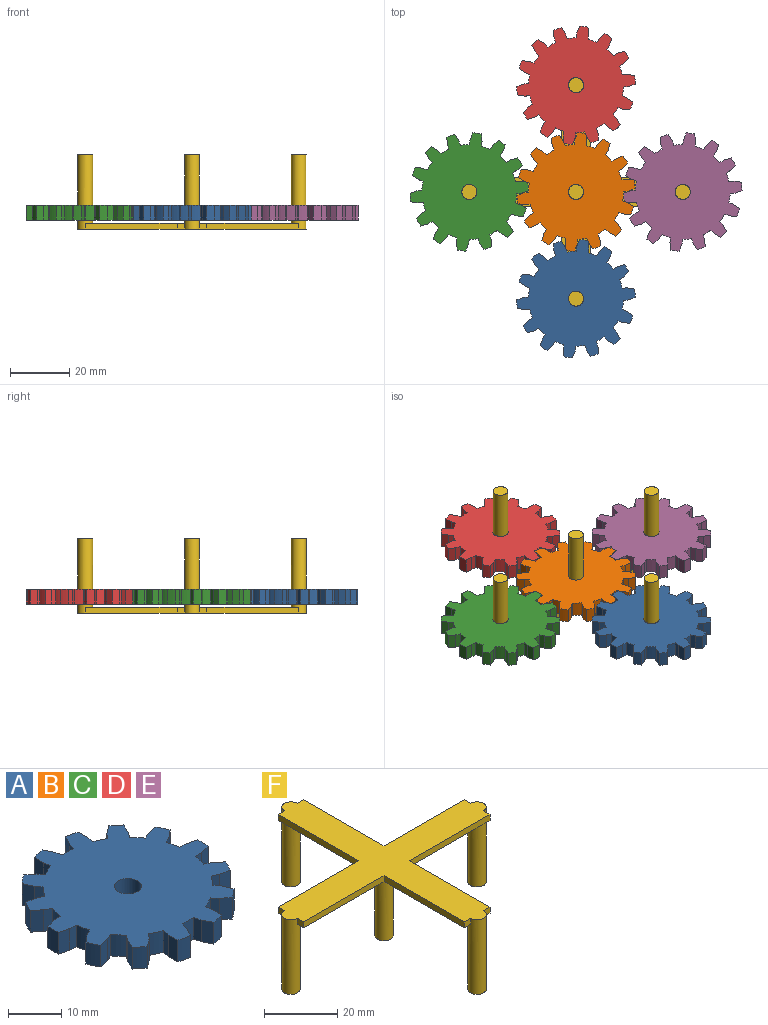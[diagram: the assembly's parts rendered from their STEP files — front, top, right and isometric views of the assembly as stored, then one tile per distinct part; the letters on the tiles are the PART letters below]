
ASSEMBLY  parts=6 mates=5
PART A: 87 faces, bbox 40x39.5x5 mm
  f0: cylinder r=20mm len=5mm, axis (0,0,-1), area 14.3mm2, adj f15,f16,f19,f83
  f1: cylinder r=20mm len=5mm, axis (0,0,-1), area 14.3mm2, adj f15,f16,f78,f84
  f2: cylinder r=20mm len=5mm, axis (0,0,-1), area 14.3mm2, adj f15,f16,f73,f79
  f3: cylinder r=20mm len=5mm, axis (0,0,-1), area 14.3mm2, adj f15,f16,f68,f74
  f4: cylinder r=20mm len=5mm, axis (0,0,-1), area 14.3mm2, adj f15,f16,f63,f69
  f5: cylinder r=20mm len=5mm, axis (0,0,-1), area 14.3mm2, adj f15,f16,f58,f64
  f6: cylinder r=20mm len=5mm, axis (0,0,-1), area 14.3mm2, adj f15,f16,f53,f59
  f7: cylinder r=20mm len=5mm, axis (0,0,-1), area 14.3mm2, adj f15,f16,f48,f54
  f8: cylinder r=20mm len=5mm, axis (0,0,-1), area 14.3mm2, adj f15,f16,f43,f49
  f9: cylinder r=20mm len=5mm, axis (0,0,-1), area 14.3mm2, adj f15,f16,f38,f44
  f10: cylinder r=20mm len=5mm, axis (0,0,-1), area 14.3mm2, adj f15,f16,f33,f39
  f11: cylinder r=20mm len=5mm, axis (0,0,-1), area 14.3mm2, adj f15,f16,f28,f34
  f12: cylinder r=20mm len=5mm, axis (0,0,-1), area 14.3mm2, adj f15,f16,f23,f29
  f13: cylinder r=20mm len=5mm, axis (0,0,-1), area 14.3mm2, adj f15,f16,f18,f24
  f14: cylinder r=2.55mm len=5.1mm, axis (0,0,-1), area 80.1mm2, adj f15,f16
  f15: plane 40x39.53mm, normal (0,0,1), area 993.6mm2, adj f0,f1,f2,f3,f4,f5,f6,f7
  f16: plane 40x39.53mm, normal (0,0,-1), area 993.6mm2, adj f0,f1,f2,f3,f4,f5,f6,f7
  f17: plane 5x1.64mm, normal (-0.97,0.25,0), area 8.5mm2, adj f15,f16,f18,f21
  f18: plane 5x2.19mm, normal (-0.89,0.46,0), area 12.3mm2, adj f13,f15,f16,f17
  f19: plane 5x2.19mm, normal (0.89,0.46,0), area 12.3mm2, adj f0,f15,f16,f20
  f20: plane 5x1.64mm, normal (0.97,0.25,0), area 8.5mm2, adj f15,f16,f19,f21
  f21: cylinder r=16mm len=5mm, axis (0,0,-1), area 15mm2, adj f15,f16,f17,f20
  f22: plane 5x1.3mm, normal (-0.77,0.64,0), area 8.5mm2, adj f15,f16,f23,f26
  f23: plane 5x1.97mm, normal (-0.6,0.8,0), area 12.3mm2, adj f12,f15,f16,f22
  f24: plane 5x2.47mm, normal (1,0.03,0), area 12.3mm2, adj f13,f15,f16,f25
  f25: plane 5x1.66mm, normal (0.98,-0.2,0), area 8.5mm2, adj f15,f16,f24,f26
  f26: cylinder r=16mm len=5mm, axis (0,0,-1), area 15mm2, adj f15,f16,f22,f25
  f27: plane 5x1.55mm, normal (-0.41,0.91,0), area 8.5mm2, adj f15,f16,f28,f31
  f28: plane 5x2.42mm, normal (-0.2,0.98,0), area 12.3mm2, adj f11,f15,f16,f27
  f29: plane 5x2.25mm, normal (0.91,-0.41,0), area 12.3mm2, adj f12,f15,f16,f30
  f30: plane 5x1.35mm, normal (0.8,-0.6,0), area 8.5mm2, adj f15,f16,f29,f31
  f31: cylinder r=16mm len=5mm, axis (0,0,-1), area 15mm2, adj f15,f16,f27,f30
  f32: plane 5x1.69mm, normal (0.03,1,0), area 8.5mm2, adj f15,f16,f33,f36
  f33: plane 5x2.39mm, normal (0.25,0.97,0), area 12.3mm2, adj f10,f15,f16,f32
  f34: plane 5x1.89mm, normal (0.64,-0.76,0), area 12.3mm2, adj f11,f15,f16,f35
  f35: plane 5x1.51mm, normal (0.46,-0.89,0), area 8.5mm2, adj f15,f16,f34,f36
  f36: cylinder r=16mm len=5mm, axis (0,0,-1), area 15mm2, adj f15,f16,f32,f35
  f37: plane 5x1.51mm, normal (0.46,0.89,0), area 8.5mm2, adj f15,f16,f38,f41
  f38: plane 5x1.89mm, normal (0.64,0.76,0), area 12.3mm2, adj f9,f15,f16,f37
  f39: plane 5x2.39mm, normal (0.25,-0.97,0), area 12.3mm2, adj f10,f15,f16,f40
  f40: plane 5x1.69mm, normal (0.03,-1,0), area 8.5mm2, adj f15,f16,f39,f41
  f41: cylinder r=16mm len=5mm, axis (0,0,-1), area 15mm2, adj f15,f16,f37,f40
  f42: plane 5x1.35mm, normal (0.8,0.6,0), area 8.5mm2, adj f15,f16,f43,f46
  f43: plane 5x2.25mm, normal (0.91,0.41,0), area 12.3mm2, adj f8,f15,f16,f42
  f44: plane 5x2.42mm, normal (-0.2,-0.98,0), area 12.3mm2, adj f9,f15,f16,f45
  f45: plane 5x1.55mm, normal (-0.41,-0.91,0), area 8.5mm2, adj f15,f16,f44,f46
  f46: cylinder r=16mm len=5mm, axis (0,0,-1), area 15mm2, adj f15,f16,f42,f45
  f47: plane 5x1.66mm, normal (0.98,0.2,0), area 8.5mm2, adj f15,f16,f48,f51
  f48: plane 5x2.47mm, normal (1,-0.03,0), area 12.3mm2, adj f7,f15,f16,f47
  f49: plane 5x1.97mm, normal (-0.6,-0.8,0), area 12.3mm2, adj f8,f15,f16,f50
  f50: plane 5x1.3mm, normal (-0.77,-0.64,0), area 8.5mm2, adj f15,f16,f49,f51
  f51: cylinder r=16mm len=5mm, axis (0,0,-1), area 15mm2, adj f15,f16,f47,f50
  f52: plane 5x1.64mm, normal (0.97,-0.25,0), area 8.5mm2, adj f15,f16,f53,f56
  f53: plane 5x2.19mm, normal (0.89,-0.46,0), area 12.3mm2, adj f6,f15,f16,f52
  f54: plane 5x2.19mm, normal (-0.89,-0.46,0), area 12.3mm2, adj f7,f15,f16,f55
  f55: plane 5x1.64mm, normal (-0.97,-0.25,0), area 8.5mm2, adj f15,f16,f54,f56
  f56: cylinder r=16mm len=5mm, axis (0,0,-1), area 15mm2, adj f15,f16,f52,f55
  f57: plane 5x1.3mm, normal (0.77,-0.64,0), area 8.5mm2, adj f15,f16,f58,f61
  f58: plane 5x1.97mm, normal (0.6,-0.8,0), area 12.3mm2, adj f5,f15,f16,f57
  f59: plane 5x2.47mm, normal (-1,-0.03,0), area 12.3mm2, adj f6,f15,f16,f60
  f60: plane 5x1.66mm, normal (-0.98,0.2,0), area 8.5mm2, adj f15,f16,f59,f61
  f61: cylinder r=16mm len=5mm, axis (0,0,-1), area 15mm2, adj f15,f16,f57,f60
  f62: plane 5x1.55mm, normal (0.41,-0.91,0), area 8.5mm2, adj f15,f16,f63,f66
  f63: plane 5x2.42mm, normal (0.2,-0.98,0), area 12.3mm2, adj f4,f15,f16,f62
  f64: plane 5x2.25mm, normal (-0.91,0.41,0), area 12.3mm2, adj f5,f15,f16,f65
  f65: plane 5x1.35mm, normal (-0.8,0.6,0), area 8.5mm2, adj f15,f16,f64,f66
  f66: cylinder r=16mm len=5mm, axis (0,0,-1), area 15mm2, adj f15,f16,f62,f65
  f67: plane 5x1.69mm, normal (-0.03,-1,0), area 8.5mm2, adj f15,f16,f68,f71
  f68: plane 5x2.39mm, normal (-0.25,-0.97,0), area 12.3mm2, adj f3,f15,f16,f67
  f69: plane 5x1.89mm, normal (-0.64,0.76,0), area 12.3mm2, adj f4,f15,f16,f70
  f70: plane 5x1.51mm, normal (-0.46,0.89,0), area 8.5mm2, adj f15,f16,f69,f71
  f71: cylinder r=16mm len=5mm, axis (0,0,-1), area 15mm2, adj f15,f16,f67,f70
  f72: plane 5x1.51mm, normal (-0.46,-0.89,0), area 8.5mm2, adj f15,f16,f73,f76
  f73: plane 5x1.89mm, normal (-0.64,-0.76,0), area 12.3mm2, adj f2,f15,f16,f72
  f74: plane 5x2.39mm, normal (-0.25,0.97,0), area 12.3mm2, adj f3,f15,f16,f75
  f75: plane 5x1.69mm, normal (-0.03,1,0), area 8.5mm2, adj f15,f16,f74,f76
  f76: cylinder r=16mm len=5mm, axis (0,0,-1), area 15mm2, adj f15,f16,f72,f75
  f77: plane 5x1.35mm, normal (-0.8,-0.6,0), area 8.5mm2, adj f15,f16,f78,f81
  f78: plane 5x2.25mm, normal (-0.91,-0.41,0), area 12.3mm2, adj f1,f15,f16,f77
  f79: plane 5x2.42mm, normal (0.2,0.98,0), area 12.3mm2, adj f2,f15,f16,f80
  f80: plane 5x1.55mm, normal (0.41,0.91,0), area 8.5mm2, adj f15,f16,f79,f81
  f81: cylinder r=16mm len=5mm, axis (0,0,-1), area 15mm2, adj f15,f16,f77,f80
  f82: plane 5x1.66mm, normal (-0.98,-0.2,0), area 8.5mm2, adj f15,f16,f83,f86
  f83: plane 5x2.47mm, normal (-1,0.03,0), area 12.3mm2, adj f0,f15,f16,f82
  f84: plane 5x1.97mm, normal (0.6,0.8,0), area 12.3mm2, adj f1,f15,f16,f85
  f85: plane 5x1.3mm, normal (0.77,0.64,0), area 8.5mm2, adj f15,f16,f84,f86
  f86: cylinder r=16mm len=5mm, axis (0,0,-1), area 15mm2, adj f15,f16,f82,f85
PART B: same geometry as A
PART C: same geometry as A
PART D: same geometry as A
PART E: same geometry as A
PART F: 28 faces, bbox 77x77x25 mm
  f0: plane 31x2mm, normal (1,0,0), area 62mm2, adj f1,f15,f16,f17
  f1: plane 2.5x2mm, normal (0,-1,0), area 5mm2, adj f0,f16,f17,f22
  f2: plane 2.5x2mm, normal (0,-1,0), area 5mm2, adj f3,f16,f17,f22
  f3: plane 31x2mm, normal (-1,0,0), area 62mm2, adj f2,f4,f16,f17
  f4: plane 31x2mm, normal (0,-1,0), area 62mm2, adj f3,f5,f16,f17
  f5: plane 2.5x2mm, normal (-1,0,0), area 5mm2, adj f4,f16,f17,f18
  f6: plane 2.5x2mm, normal (-1,0,0), area 5mm2, adj f7,f16,f17,f18
  f7: plane 31x2mm, normal (0,1,0), area 62mm2, adj f6,f8,f16,f17
  f8: plane 31x2mm, normal (-1,0,0), area 62mm2, adj f7,f9,f16,f17
  f9: plane 2.5x2mm, normal (0,1,0), area 5mm2, adj f8,f16,f17,f24
  f10: plane 2.5x2mm, normal (0,1,0), area 5mm2, adj f11,f16,f17,f24
  f11: plane 31x2mm, normal (1,0,0), area 62mm2, adj f10,f12,f16,f17
  f12: plane 31x2mm, normal (0,1,0), area 62mm2, adj f11,f13,f16,f17
  f13: plane 2.5x2mm, normal (1,0,0), area 5mm2, adj f12,f16,f17,f20
  f14: plane 2.5x2mm, normal (1,0,0), area 5mm2, adj f15,f16,f17,f20
  f15: plane 31x2mm, normal (0,-1,0), area 62mm2, adj f0,f14,f16,f17
  f16: plane 72x72mm, normal (0,0,-1), area 1281.1mm2, adj f0,f1,f2,f3,f4,f5,f6,f7
  f17: plane 77x77mm, normal (0,0,1), area 1379.3mm2, adj f0,f1,f2,f3,f4,f5,f6,f7
  f18: cylinder r=2.5mm len=25mm, axis (0,0,1), area 377mm2, adj f5,f6,f16,f17,f19
  f19: plane 5x5mm, normal (0,0,-1), area 19.6mm2, adj f18
  f20: cylinder r=2.5mm len=25mm, axis (0,0,1), area 377mm2, adj f13,f14,f16,f17,f21
  f21: plane 5x5mm, normal (0,0,-1), area 19.6mm2, adj f20
  f22: cylinder r=2.5mm len=25mm, axis (0,0,1), area 377mm2, adj f1,f2,f16,f17,f23
  f23: plane 5x5mm, normal (0,0,-1), area 19.6mm2, adj f22
  f24: cylinder r=2.5mm len=25mm, axis (0,0,1), area 377mm2, adj f9,f10,f16,f17,f25
  f25: plane 5x5mm, normal (0,0,-1), area 19.6mm2, adj f24
  f26: cylinder r=2.5mm len=23mm, axis (0,0,1), area 361.3mm2, adj f16,f27
  f27: plane 5x5mm, normal (0,0,-1), area 19.6mm2, adj f26
PLACE A rot(axis=(-0.39,-0.92,0),180deg) t=(86.62,56.17,42.87)mm
PLACE B rot(axis=(-0.37,-0.93,0),180deg) t=(86.62,92.17,42.87)mm
PLACE C rot(axis=(0,0,-1),46.1deg) t=(50.62,92.17,37.87)mm
PLACE D rot(axis=(0,0,1),133.9deg) t=(86.62,128.17,37.87)mm
PLACE E rot(axis=(0,0,1),133.9deg) t=(122.62,92.17,37.87)mm
PLACE F rot(axis=(0,1,0),180deg) t=(86.62,92.17,34.87)mm fixed
MATE revolute C.f14 <-> F.f20  axis (0,0,-1) through (50.62,92.17,37.87)mm
MATE revolute A.f14 <-> F.f22  axis (0,0,-1) through (86.62,56.17,37.87)mm
MATE revolute E.f14 <-> F.f18  axis (0,0,-1) through (122.62,92.17,37.87)mm
MATE revolute D.f14 <-> F.f24  axis (0,0,-1) through (86.62,128.17,37.87)mm
MATE revolute B.f14 <-> F.f26  axis (0,0,-1) through (86.62,92.17,37.87)mm
